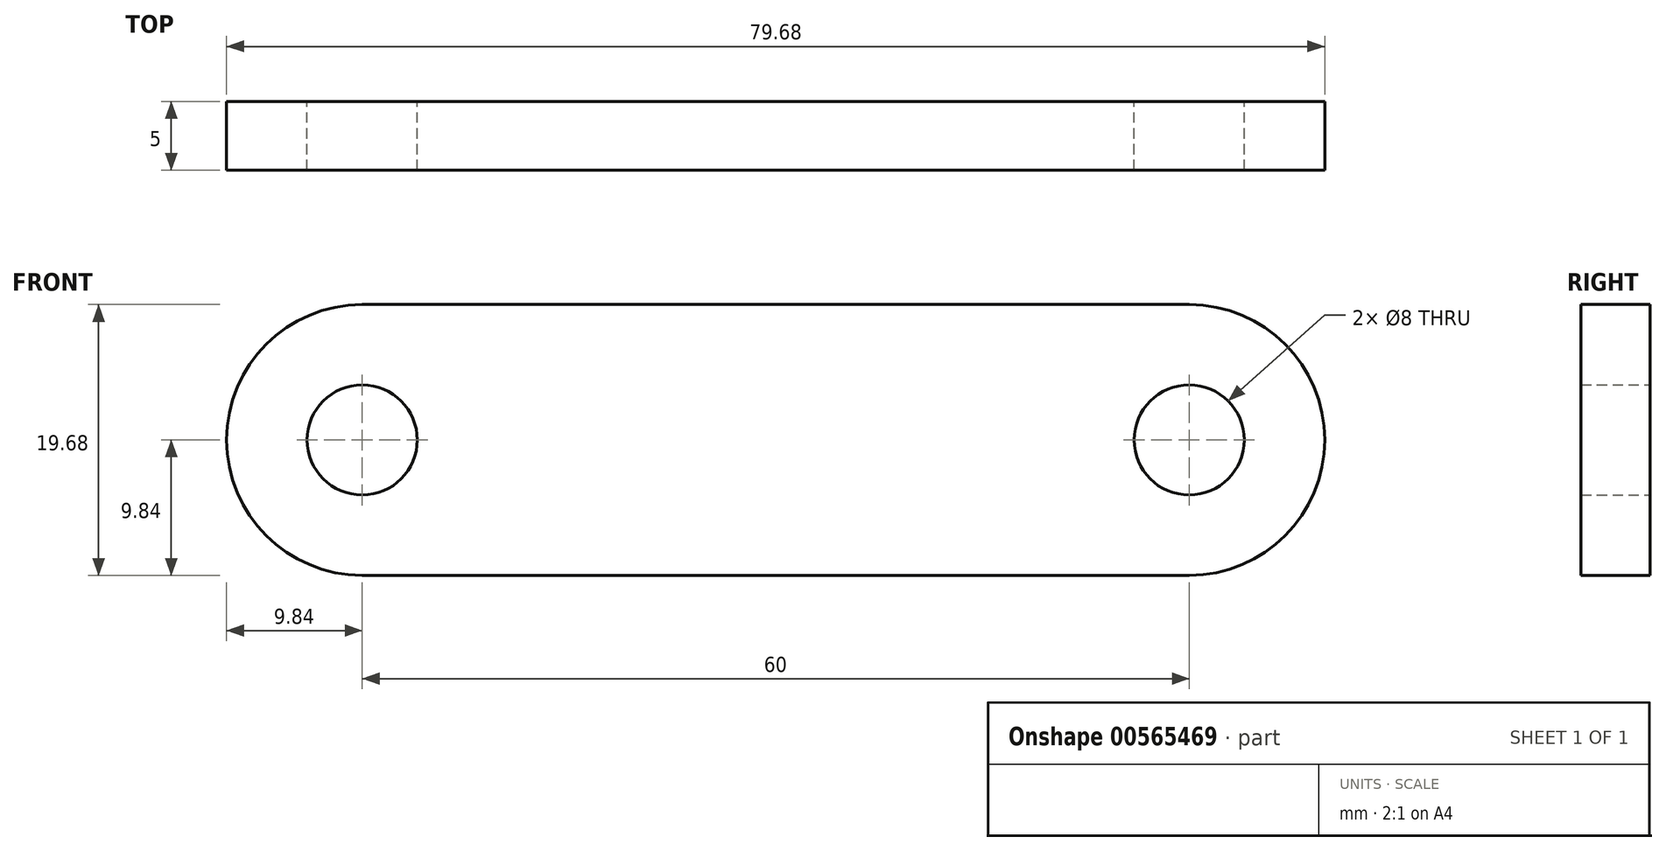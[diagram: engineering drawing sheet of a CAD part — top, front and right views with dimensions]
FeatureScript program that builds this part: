
annotation { "Feature Type Name" : "Feature", "Feature Type Description" : "" }
export const myFeature = defineFeature(function(context is Context, id is Id, definition is map)
    precondition{}
    {
        {
            var Q0;
            Q0=qCreatedBy(makeId("Front.planeOp"),FACE);
            var sketch = newSketch(context, id + "F0", { "sketchPlane" : qUnion([Q0])});
            skArc(sketch, "E0", {"start": v(-30, 9.84) * mm, "mid": v(-39.84, 0) * mm, "end": v(-30, -9.84) * mm});
            skLineSegment(sketch, "E1", {"start": v(-30, 9.84) * mm, "end": v(0, 9.84) * mm});
            skLineSegment(sketch, "E2", {"start": v(-30, -9.84) * mm, "end": v(0, -9.83) * mm});
            skLineSegment(sketch, "E3.MirrorCS", {"start": v(30, 9.84) * mm, "end": v(0, 9.84) * mm});
            skArc(sketch, "E4.MirrorCS", {"start": v(30, 9.84) * mm, "mid": v(39.84, 0) * mm, "end": v(30, -9.84) * mm});
            skLineSegment(sketch, "E5.MirrorCS", {"start": v(30, -9.84) * mm, "end": v(0, -9.83) * mm});
            skCircle(sketch, "E6", {"center": v(-30, 0) * mm, "radius": 4 * mm});
            skCircle(sketch, "E7", {"center": v(30, 0) * mm, "radius": 4 * mm});
            skSolve(sketch);
        }
        {
            var Q0;
            Q0 = qSketchRegion(id + "F0", true);
            extrude(context, id + "F1", {"entities" : qUnion([Q0]), "endBound" : BoundingType.SYMMETRIC, "depth" : 5 * mm, "offsetDistance" : 25.4 * mm});
        }
    });
